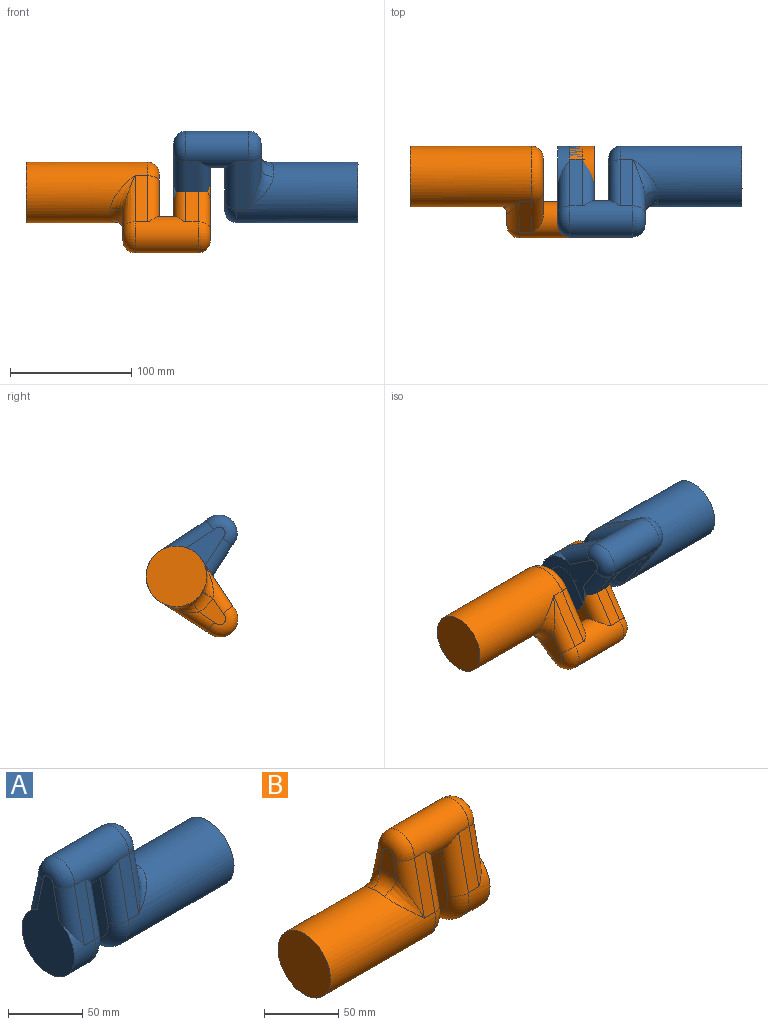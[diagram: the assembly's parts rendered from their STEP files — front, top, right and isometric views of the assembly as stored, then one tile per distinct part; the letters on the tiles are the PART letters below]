
ASSEMBLY  parts=2 mates=1
PART A: 27 faces, bbox 152x54.1x92.1 mm
  f0: cylinder r=25mm len=50mm, axis (-1,0,0), area 1955.6mm2, adj f14,f15,f17,f19,f22,f26
  f1: cylinder r=15mm len=52mm, axis (1,0,0), area 3207.9mm2, adj f4,f5,f6,f9,f14,f15,f16,f18
  f2: cylinder r=25mm len=100mm, axis (1,0,0), area 14088.7mm2, adj f3,f4,f5,f11,f12,f13,f24
  f3: plane 50x50mm, normal (1,0,0), area 1963.5mm2, adj f2
  f4: plane 44.84x10mm, normal (0,-0.98,0.21), area 458.3mm2, adj f1,f2,f10,f23
  f5: plane 44.84x10mm, normal (0,0.98,0.21), area 458.3mm2, adj f1,f2,f8,f25
  f6: plane 52.02x30mm, normal (-1,0,0), area 1178.1mm2, adj f1,f23,f24,f25
  f7: plane 20.96x16.3mm, normal (1,0,0), area 235.3mm2, adj f8,f9,f10,f12
  f8: cylinder r=10mm len=48.2mm, axis (0,-0.21,0.98), area 441.4mm2, adj f5,f7,f9,f13
  f9: torus R=5mm, axis (-1,0,0), area 571.1mm2, adj f1,f7,f8,f10
  f10: cylinder r=10mm len=48.2mm, axis (0,-0.21,-0.98), area 441.4mm2, adj f4,f7,f9,f11
  f11: bspline ~30.01x21.54mm, area 262.1mm2, adj f2,f10,f12
  f12: torus R=35mm, axis (-1,0,0), area 211.4mm2, adj f2,f7,f11,f13
  f13: bspline ~30.01x21.54mm, area 262.1mm2, adj f2,f8,f12
  f14: plane 44.84x10mm, normal (0,-0.98,0.21), area 458.3mm2, adj f0,f1,f19,f20
  f15: plane 44.84x10mm, normal (0,0.98,0.21), area 458.3mm2, adj f0,f1,f17,f21
  f16: plane 52.02x30mm, normal (1,0,0), area 1178.1mm2, adj f1,f20,f21,f22
  f17: cylinder r=10mm len=48.2mm, axis (0,-0.21,0.98), area 551.6mm2, adj f0,f15,f18,f26
  f18: torus R=5mm, axis (1,0,0), area 571.1mm2, adj f1,f17,f19,f26
  f19: cylinder r=10mm len=48.2mm, axis (0,-0.21,-0.98), area 551.6mm2, adj f0,f14,f18,f26
  f20: cylinder r=10mm len=46.9mm, axis (0,0.21,0.98), area 627.6mm2, adj f1,f14,f16,f22
  f21: cylinder r=10mm len=46.9mm, axis (0,0.21,-0.98), area 627.6mm2, adj f1,f15,f16,f22
  f22: torus R=15mm, axis (1,0,0), area 1194mm2, adj f0,f16,f20,f21
  f23: cylinder r=10mm len=46.9mm, axis (0,0.21,0.98), area 627.6mm2, adj f1,f4,f6,f24
  f24: torus R=15mm, axis (-1,0,0), area 1194mm2, adj f2,f6,f23,f25
  f25: cylinder r=10mm len=46.9mm, axis (0,0.21,-0.98), area 627.6mm2, adj f1,f5,f6,f24
  f26: plane 80x50mm, normal (-1,0,0), area 2388.8mm2, adj f0,f17,f18,f19
PART B: 27 faces, bbox 152x54.1x92.1 mm
  f0: cylinder r=25mm len=50mm, axis (1,0,0), area 1955.6mm2, adj f14,f15,f17,f19,f22,f26
  f1: cylinder r=15mm len=52mm, axis (-1,0,0), area 3207.9mm2, adj f4,f5,f6,f9,f14,f15,f16,f18
  f2: cylinder r=25mm len=100mm, axis (-1,0,0), area 14088.7mm2, adj f3,f4,f5,f11,f12,f13,f24
  f3: plane 50x50mm, normal (-1,0,0), area 1963.5mm2, adj f2
  f4: plane 44.84x10mm, normal (0,-0.98,0.21), area 458.3mm2, adj f1,f2,f10,f23
  f5: plane 44.84x10mm, normal (0,0.98,0.21), area 458.3mm2, adj f1,f2,f8,f25
  f6: plane 52.02x30mm, normal (1,0,0), area 1178.1mm2, adj f1,f23,f24,f25
  f7: plane 20.96x16.3mm, normal (-1,0,0), area 235.3mm2, adj f8,f9,f10,f12
  f8: cylinder r=10mm len=48.2mm, axis (0,-0.21,0.98), area 441.4mm2, adj f5,f7,f9,f13
  f9: torus R=5mm, axis (1,0,0), area 571.1mm2, adj f1,f7,f8,f10
  f10: cylinder r=10mm len=48.2mm, axis (0,-0.21,-0.98), area 441.4mm2, adj f4,f7,f9,f11
  f11: bspline ~29.5x20.09mm, area 262.1mm2, adj f2,f10,f12
  f12: torus R=35mm, axis (1,0,0), area 211.4mm2, adj f2,f7,f11,f13
  f13: bspline ~29.5x20.09mm, area 262.1mm2, adj f2,f8,f12
  f14: plane 44.84x10mm, normal (0,-0.98,0.21), area 458.3mm2, adj f0,f1,f19,f20
  f15: plane 44.84x10mm, normal (0,0.98,0.21), area 458.3mm2, adj f0,f1,f17,f21
  f16: plane 52.02x30mm, normal (-1,0,0), area 1178.1mm2, adj f1,f20,f21,f22
  f17: cylinder r=10mm len=48.2mm, axis (0,-0.21,0.98), area 551.6mm2, adj f0,f15,f18,f26
  f18: torus R=5mm, axis (-1,0,0), area 571.1mm2, adj f1,f17,f19,f26
  f19: cylinder r=10mm len=48.2mm, axis (0,-0.21,-0.98), area 551.6mm2, adj f0,f14,f18,f26
  f20: cylinder r=10mm len=46.9mm, axis (0,0.21,0.98), area 627.6mm2, adj f1,f14,f16,f22
  f21: cylinder r=10mm len=46.9mm, axis (0,0.21,-0.98), area 627.6mm2, adj f1,f15,f16,f22
  f22: torus R=15mm, axis (-1,0,0), area 1194mm2, adj f0,f16,f20,f21
  f23: cylinder r=10mm len=46.9mm, axis (0,0.21,0.98), area 627.6mm2, adj f1,f4,f6,f24
  f24: torus R=15mm, axis (1,0,0), area 1194mm2, adj f2,f6,f23,f25
  f25: cylinder r=10mm len=46.9mm, axis (0,0.21,-0.98), area 627.6mm2, adj f1,f5,f6,f24
  f26: plane 80x50mm, normal (1,0,0), area 2388.8mm2, adj f0,f17,f18,f19
PLACE A rot(axis=(1,0,0),44.6deg) t=(1.86,0.84,3.47)mm
PLACE B rot(axis=(1,0,0),134.6deg) t=(81.86,0.84,3.47)mm
MATE fastened B.f0 <-> A.f0  axis (1,0,0) through (233.86,0.84,3.47)mm
